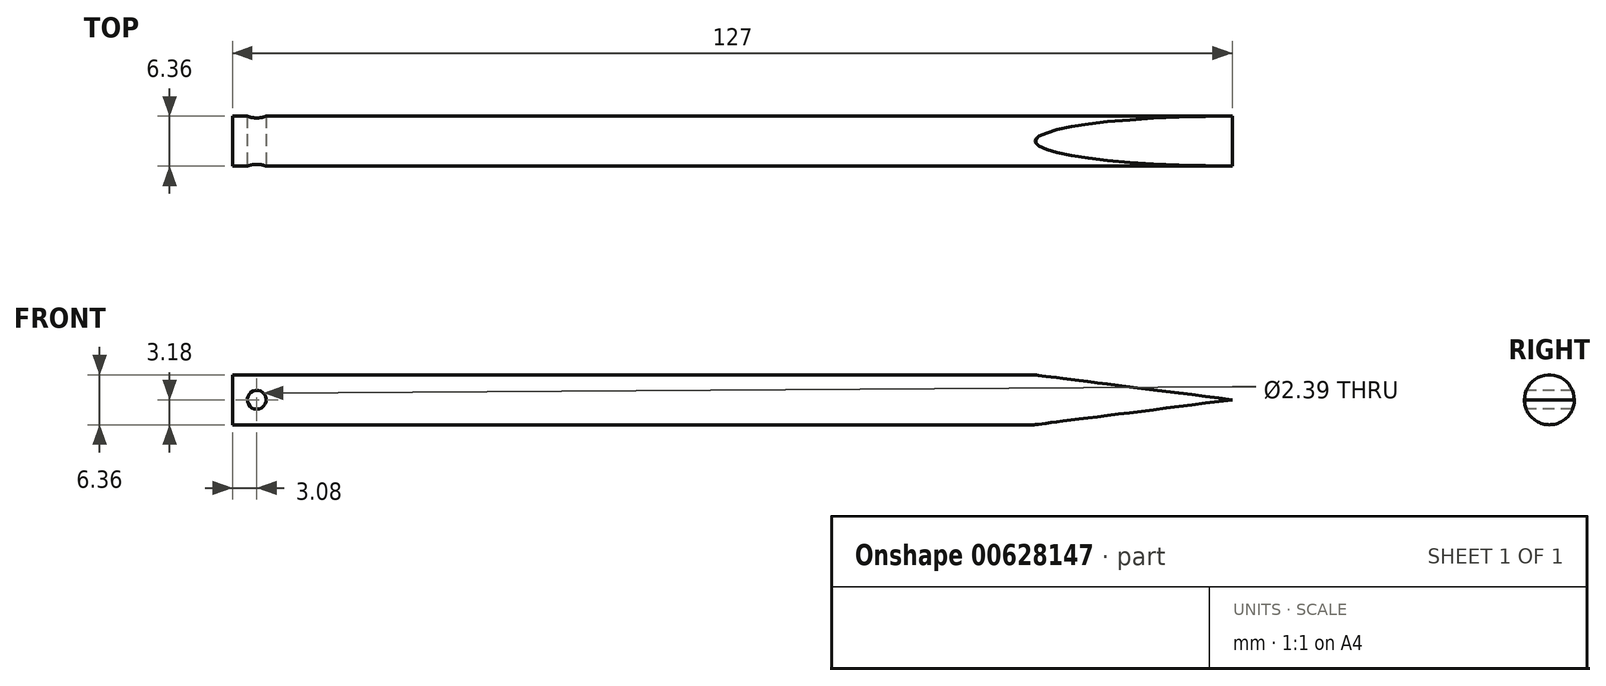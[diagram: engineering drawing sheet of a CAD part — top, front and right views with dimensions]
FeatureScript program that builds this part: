
annotation { "Feature Type Name" : "Feature", "Feature Type Description" : "" }
export const myFeature = defineFeature(function(context is Context, id is Id, definition is map)
    precondition{}
    {
        {
            var Q0;
            Q0=qCreatedBy(makeId("Right.planeOp"),FACE);
            var sketch = newSketch(context, id + "F0", { "sketchPlane" : qUnion([Q0])});
            skCircle(sketch, "E0", {"center": v(0, 0) * mm, "radius": 3.18 * mm});
            skSolve(sketch);
        }
        {
            var Q0;
            Q0 = qSketchRegion(id + "F0", true);
            extrude(context, id + "F1", {"entities" : qUnion([Q0]), "oppositeDirection" : true, "depth" : 127 * mm, "offsetDistance" : 25.4 * mm});
        }
        {
            var Q0;
            Q0=qCreatedBy(makeId("Front.planeOp"),FACE);
            var sketch = newSketch(context, id + "F2", { "sketchPlane" : qUnion([Q0])});
            skLineSegment(sketch, "E1", {"start": v(-25.2, 3.18) * mm, "end": v(0, 0) * mm});
            skLineSegment(sketch, "E2", {"start": v(-25.2, 3.18) * mm, "end": v(-25.2, 5.16) * mm});
            skLineSegment(sketch, "E3", {"start": v(-25.2, 5.16) * mm, "end": v(0, 5.16) * mm});
            skLineSegment(sketch, "E4", {"start": v(0, 5.16) * mm, "end": v(0, 0) * mm});
            skLineSegment(sketch, "E5", {"start": v(-25.2, 0) * mm, "end": v(0, 0) * mm});
            skPoint(sketch, "E5.startSnap0", {"position": v(-25.2, 4.17) * mm});
            skLineSegment(sketch, "E6.MirrorCS", {"start": v(-25.2, -3.18) * mm, "end": v(-25.2, -5.16) * mm});
            skLineSegment(sketch, "E7.MirrorCS", {"start": v(-25.2, -5.16) * mm, "end": v(0, -5.16) * mm});
            skPoint(sketch, "E8.MirrorP", {"position": v(-25.2, -4.17) * mm});
            skLineSegment(sketch, "E9.MirrorCS", {"start": v(0, -5.16) * mm, "end": v(0, 0) * mm});
            skLineSegment(sketch, "E10.MirrorCS", {"start": v(-25.2, -3.18) * mm, "end": v(0, 0) * mm});
            skCircle(sketch, "E11", {"center": v(-123.92, 0) * mm, "radius": 1.2 * mm});
            skSolve(sketch);
        }
        {
            var Q0;
            Q0 = qSketchRegion(id + "F2", true);
            extrude(context, id + "F3", {"entities" : qUnion([Q0]), "operationType" : NewBodyOperationType.REMOVE, "endBound" : BoundingType.SYMMETRIC, "oppositeDirection" : true, "depth" : 25.4 * mm, "offsetDistance" : 25.4 * mm});
        }
    });
